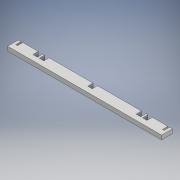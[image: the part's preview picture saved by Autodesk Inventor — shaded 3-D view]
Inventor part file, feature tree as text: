
AUTODESK INVENTOR PART (.ipt)
format: ipt  version: 2017 (Build 210142000, 142)  size: 137,728 bytes
history: native  units: mm
features: extrude x1, sketch x1
ambient origin geometry x8: Origin, YZ Plane, XZ Plane, XY Plane, X Axis, Y Axis, Z Axis, Center Point
bodies: Solid1 (feature_tree)
feature tree (2):
  extrude  "Extrusion1"  Depth=20.0mm
  sketch  "Sketch1"  dims[d4=3.2mm d5=20.0mm d6=10.0mm d7=0.0mm d8=82.0mm d9=0.0mm d10=135.0mm d11=20.0mm d12=5.0mm d13=8.2mm d14=8.2mm d15=4.1mm d16=50.0mm d17=8.0mm d18=0.0mm]
